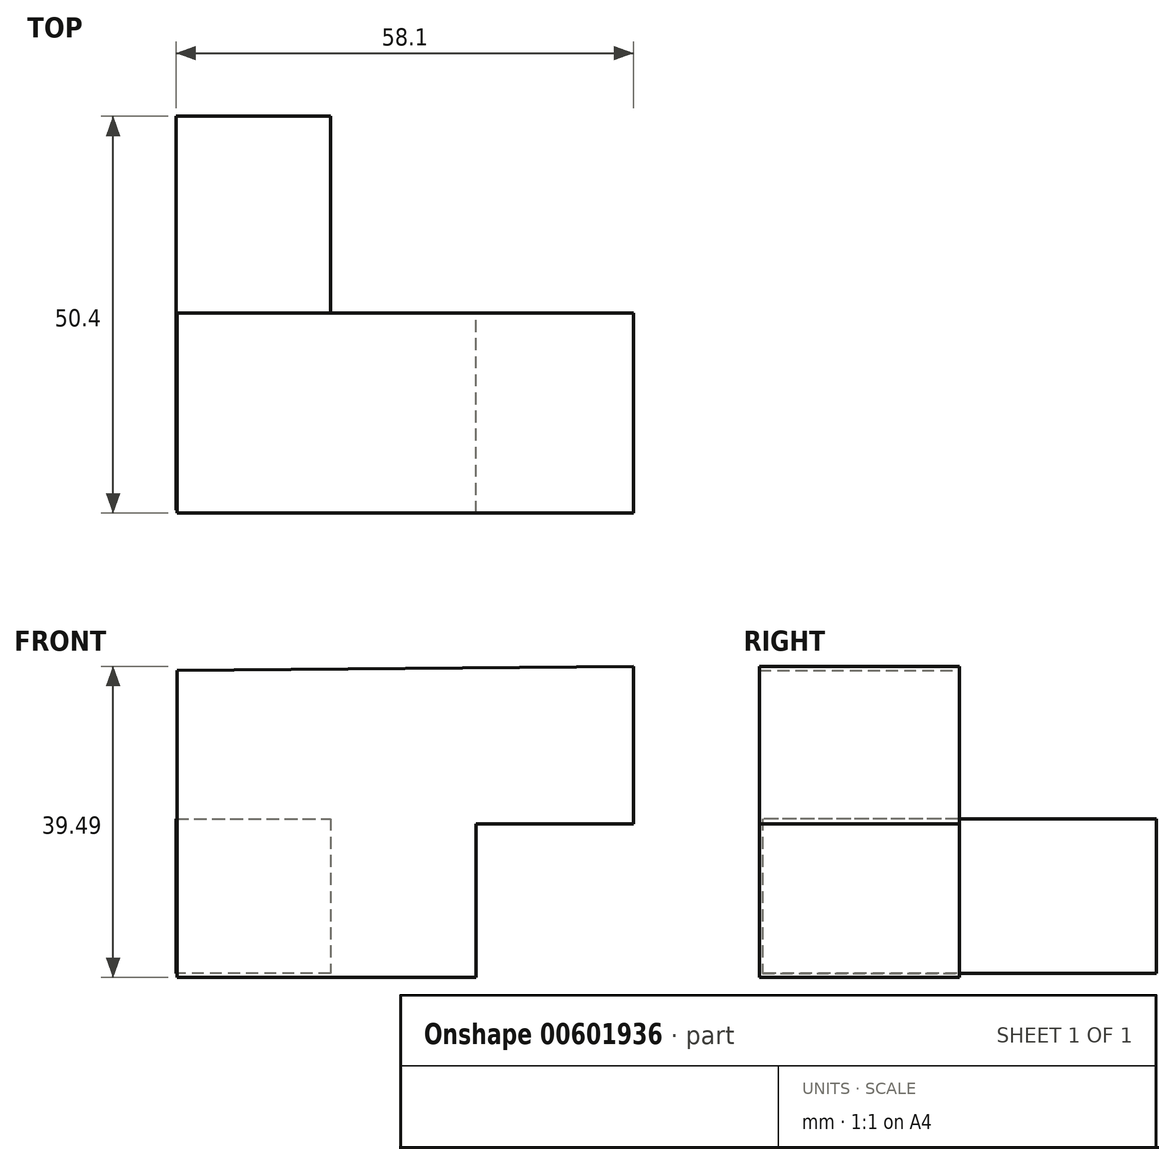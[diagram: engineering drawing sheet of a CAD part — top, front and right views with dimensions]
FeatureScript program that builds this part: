
annotation { "Feature Type Name" : "Feature", "Feature Type Description" : "" }
export const myFeature = defineFeature(function(context is Context, id is Id, definition is map)
    precondition{}
    {
        {
            var Q0;
            Q0=qCreatedBy(makeId("Front.planeOp"),FACE);
            var sketch = newSketch(context, id + "F0", { "sketchPlane" : qUnion([Q0])});
            skLineSegment(sketch, "E0", {"start": v(-21.68, 28.43) * mm, "end": v(-21.68, -10.57) * mm});
            skLineSegment(sketch, "E1", {"start": v(-21.68, -10.57) * mm, "end": v(16.32, -10.57) * mm});
            skLineSegment(sketch, "E2", {"start": v(16.32, -10.57) * mm, "end": v(16.32, 8.92) * mm});
            skLineSegment(sketch, "E3", {"start": v(16.32, 8.92) * mm, "end": v(36.31, 8.92) * mm});
            skLineSegment(sketch, "E4", {"start": v(36.31, 8.92) * mm, "end": v(36.31, 28.92) * mm});
            skLineSegment(sketch, "E5", {"start": v(36.31, 28.92) * mm, "end": v(-21.68, 28.43) * mm});
            skSolve(sketch);
        }
        {
            var Q0;
            Q0 = qSketchRegion(id + "F0", true);
            extrude(context, id + "F1", {"entities" : qUnion([Q0]), "depth" : 25.4 * mm, "offsetDistance" : 25.4 * mm});
        }
        {
            var Q0;
            Q0=qCreatedBy(makeId("Front.planeOp"),FACE);
            var sketch = newSketch(context, id + "F2", { "sketchPlane" : qUnion([Q0])});
            skLineSegment(sketch, "E6", {"start": v(-21.8, -10.06) * mm, "end": v(-21.8, 9.56) * mm});
            skLineSegment(sketch, "E7", {"start": v(-21.8, 9.56) * mm, "end": v(-2.17, 9.56) * mm});
            skLineSegment(sketch, "E8", {"start": v(-2.17, 9.56) * mm, "end": v(-2.17, -10.06) * mm});
            skLineSegment(sketch, "E9", {"start": v(-2.17, -10.06) * mm, "end": v(-21.8, -10.06) * mm});
            skSolve(sketch);
        }
        {
            var Q0;
            Q0 = qSketchRegion(id + "F2", true);
            extrude(context, id + "F3", {"entities" : qUnion([Q0]), "operationType" : NewBodyOperationType.ADD, "oppositeDirection" : true, "depth" : 25 * mm, "offsetDistance" : 25 * mm});
        }
        {
            var Q0;
            Q0 = qSketchRegion(id + "F2", true);
            extrude(context, id + "F4", {"entities" : qUnion([Q0]), "operationType" : NewBodyOperationType.ADD, "depth" : 25 * mm, "offsetDistance" : 25 * mm});
        }
    });
